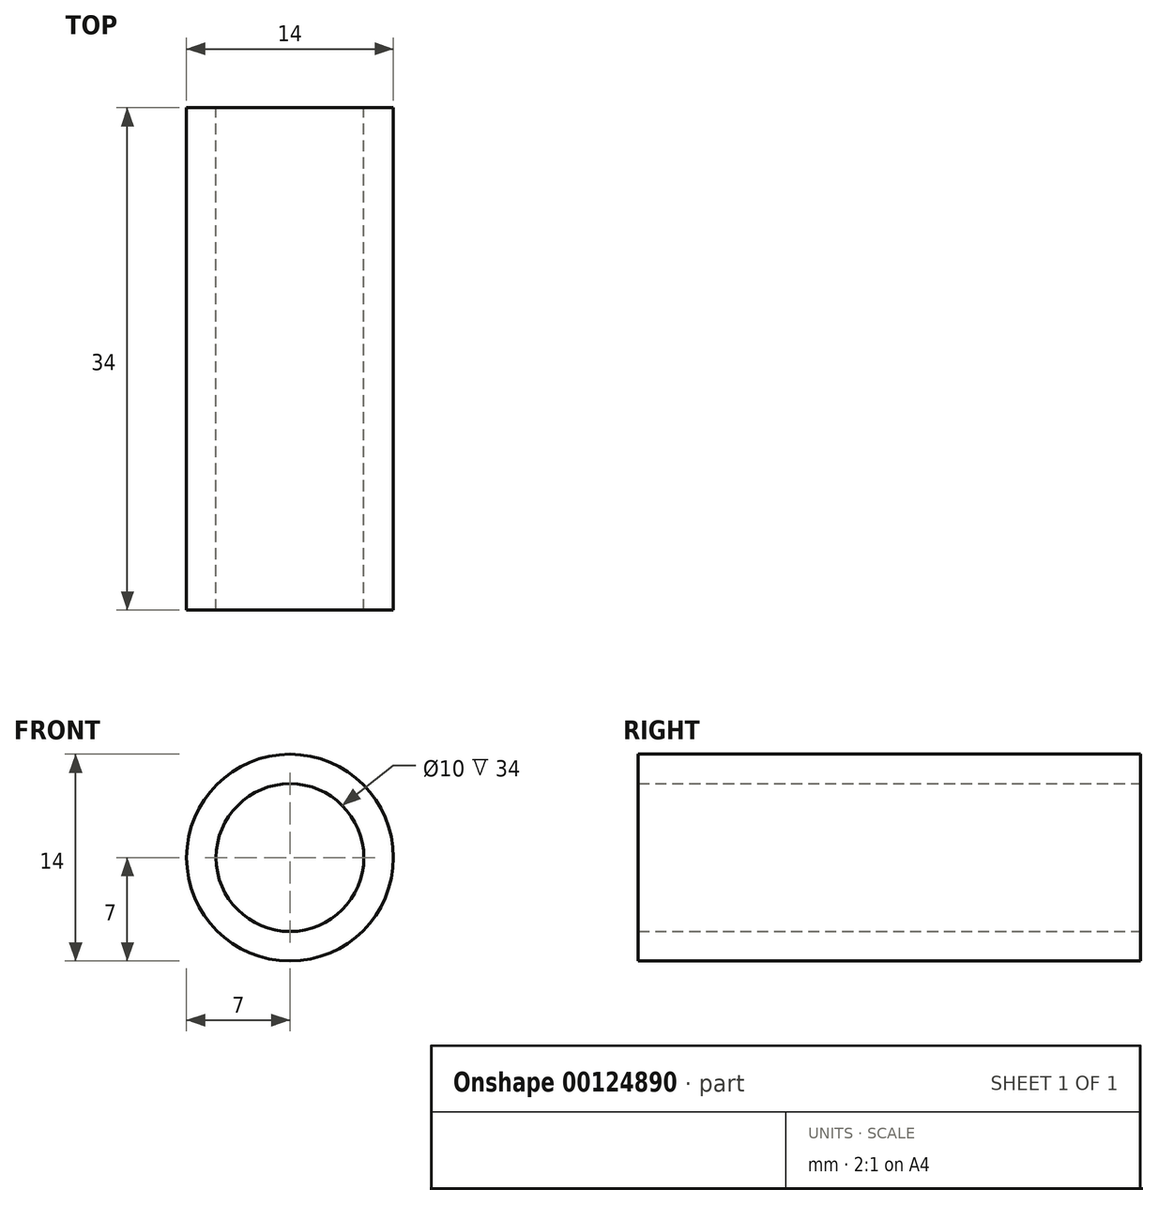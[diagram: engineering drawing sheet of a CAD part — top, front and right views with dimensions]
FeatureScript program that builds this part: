
annotation { "Feature Type Name" : "Feature", "Feature Type Description" : "" }
export const myFeature = defineFeature(function(context is Context, id is Id, definition is map)
    precondition{}
    {
        {
            var Q0;
            Q0=qCreatedBy(makeId("Front.planeOp"),FACE);
            var sketch = newSketch(context, id + "F0", { "sketchPlane" : qUnion([Q0])});
            skCircle(sketch, "E0", {"center": v(0, 0) * mm, "radius": 7 * mm});
            skCircle(sketch, "E1.0", {"center": v(0, 0) * mm, "radius": 5 * mm});
            skSolve(sketch);
        }
        {
            var Q0;
            Q0=makeQuery(id+"F0.imprint","IMPRINT",FACE,{"disambiguationData":[TD([[makeQuery(id+"F0.imprint","IMPRINT",EDGE,{"derivedFrom":sQuery(id+"F0.wireOp",EDGE,"E0")}),1.0]])]});
            extrude(context, id + "F1", {"entities" : qUnion([Q0]), "endBound" : BoundingType.SYMMETRIC, "depth" : 34 * mm});
        }
    });
